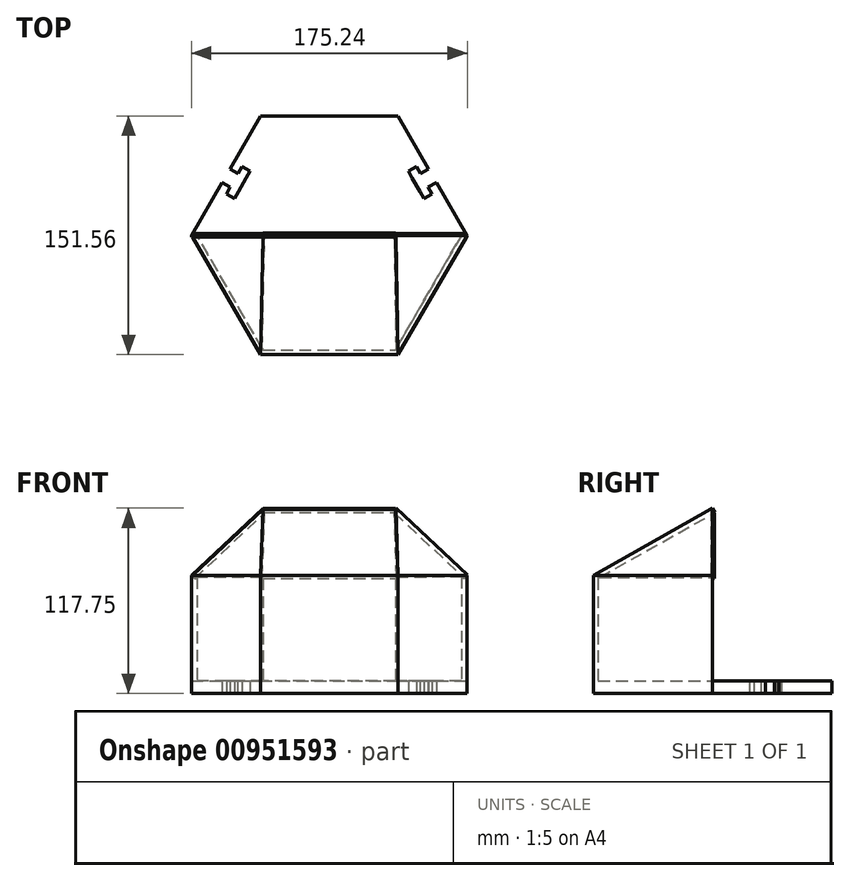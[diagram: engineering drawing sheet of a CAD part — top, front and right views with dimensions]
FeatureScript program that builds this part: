
annotation { "Feature Type Name" : "Feature", "Feature Type Description" : "" }
export const myFeature = defineFeature(function(context is Context, id is Id, definition is map)
    precondition{}
    {
        {
            var Q0;
            Q0=qCreatedBy(makeId("Top.planeOp"),FACE);
            var sketch = newSketch(context, id + "F0", { "sketchPlane" : qUnion([Q0])});
            skCircle(sketch, "E0.cCircle", {"center": v(0, 0) * mm, "radius": 75.78 * mm, "construction": true});
            skLineSegment(sketch, "E0.0", {"start": v(-43.75, 75.78) * mm, "end": v(43.75, 75.78) * mm});
            skLineSegment(sketch, "E0.1", {"start": v(43.75, 75.78) * mm, "end": v(87.5, 0) * mm});
            skLineSegment(sketch, "E0.2", {"start": v(87.5, 0) * mm, "end": v(43.75, -75.78) * mm});
            skLineSegment(sketch, "E0.3", {"start": v(43.75, -75.78) * mm, "end": v(-43.75, -75.78) * mm});
            skLineSegment(sketch, "E0.4", {"start": v(-43.75, -75.78) * mm, "end": v(-87.5, 0) * mm});
            skLineSegment(sketch, "E0.5", {"start": v(-87.5, 0) * mm, "end": v(-43.75, 75.78) * mm});
            skPoint(sketch, "E0.0.midPoint", {"position": v(0, 75.78) * mm});
            skLineSegment(sketch, "E1.0", {"start": v(-84.04, 0) * mm, "end": v(-42.02, 72.78) * mm});
            skLineSegment(sketch, "E1.1", {"start": v(42.02, 72.78) * mm, "end": v(84.04, 0) * mm});
            skLineSegment(sketch, "E1.2", {"start": v(84.04, 0) * mm, "end": v(42.02, -72.78) * mm});
            skLineSegment(sketch, "E1.3", {"start": v(-42.02, 72.78) * mm, "end": v(42.02, 72.78) * mm});
            skLineSegment(sketch, "E1.4", {"start": v(42.02, -72.78) * mm, "end": v(-42.02, -72.78) * mm});
            skLineSegment(sketch, "E1.5", {"start": v(-42.02, -72.78) * mm, "end": v(-84.04, 0) * mm});
            skLineSegment(sketch, "E2", {"start": v(-87.5, 0) * mm, "end": v(-84.04, 0) * mm});
            skLineSegment(sketch, "E3", {"start": v(84.04, 0) * mm, "end": v(87.5, 0) * mm});
            skLineSegment(sketch, "E4", {"start": v(0, 0) * mm, "end": v(0, 72.78) * mm, "construction": true});
            skLineSegment(sketch, "E5", {"start": v(0, 0) * mm, "end": v(42.02, 72.78) * mm, "construction": true});
            skLineSegment(sketch, "E6", {"start": v(0, 0) * mm, "end": v(-42.02, 72.78) * mm, "construction": true});
            skLineSegment(sketch, "E7", {"start": v(0, 36.39) * mm, "end": v(0, 72.78) * mm, "construction": true});
            skLineSegment(sketch, "E8.bottom", {"start": v(25, 48.33) * mm, "end": v(-25, 48.33) * mm});
            skLineSegment(sketch, "E8.top", {"start": v(25, 60.83) * mm, "end": v(-25, 60.83) * mm});
            skLineSegment(sketch, "E8.left", {"start": v(25, 48.33) * mm, "end": v(25, 60.83) * mm});
            skLineSegment(sketch, "E8.right", {"start": v(-25, 48.33) * mm, "end": v(-25, 60.83) * mm});
            skPoint(sketch, "E8.middle", {"position": v(0, 54.58) * mm});
            skLineSegment(sketch, "E9", {"start": v(-65.63, 37.89) * mm, "end": v(-55.16, 32) * mm, "construction": true});
            skLineSegment(sketch, "E10", {"start": v(-55.16, 32) * mm, "end": v(-52.71, 36.37) * mm, "construction": true});
            skLineSegment(sketch, "E11", {"start": v(-55.16, 32) * mm, "end": v(-57.62, 27.65) * mm, "construction": true});
            skLineSegment(sketch, "E12", {"start": v(-52.71, 36.37) * mm, "end": v(-63.12, 42.22) * mm});
            skLineSegment(sketch, "E13", {"start": v(-57.62, 27.65) * mm, "end": v(-52.71, 36.37) * mm});
            skLineSegment(sketch, "E14", {"start": v(-65.63, 37.89) * mm, "end": v(-68.13, 33.56) * mm});
            skLineSegment(sketch, "E15", {"start": v(-57.62, 27.65) * mm, "end": v(-68.13, 33.56) * mm});
            skLineSegment(sketch, "E16.MirrorCS", {"start": v(55.16, 32) * mm, "end": v(57.62, 27.65) * mm});
            skLineSegment(sketch, "E17.MirrorCS", {"start": v(55.16, 32) * mm, "end": v(52.71, 36.37) * mm});
            skLineSegment(sketch, "E18.MirrorCS", {"start": v(57.62, 27.65) * mm, "end": v(68.13, 33.56) * mm});
            skLineSegment(sketch, "E19.MirrorCS", {"start": v(87.5, 0) * mm, "end": v(43.75, 75.78) * mm});
            skLineSegment(sketch, "E20.MirrorCS", {"start": v(52.71, 36.37) * mm, "end": v(63.12, 42.22) * mm});
            skLineSegment(sketch, "E21", {"start": v(-62.87, 30.6) * mm, "end": v(-65.32, 26.25) * mm});
            skLineSegment(sketch, "E22", {"start": v(-57.62, 27.65) * mm, "end": v(-60.07, 23.3) * mm});
            skLineSegment(sketch, "E23", {"start": v(-65.32, 26.25) * mm, "end": v(-60.07, 23.3) * mm});
            skLineSegment(sketch, "E24.MirrorCS", {"start": v(-52.71, 36.37) * mm, "end": v(-50.26, 40.72) * mm});
            skLineSegment(sketch, "E25.MirrorCS", {"start": v(-57.97, 39.32) * mm, "end": v(-55.52, 43.68) * mm});
            skLineSegment(sketch, "E26.MirrorCS", {"start": v(-55.52, 43.68) * mm, "end": v(-50.26, 40.72) * mm});
            skLineSegment(sketch, "E27.MirrorCS", {"start": v(57.97, 39.32) * mm, "end": v(55.52, 43.68) * mm});
            skLineSegment(sketch, "E28.MirrorCS", {"start": v(55.52, 43.68) * mm, "end": v(50.26, 40.72) * mm});
            skLineSegment(sketch, "E29.MirrorCS", {"start": v(52.71, 36.37) * mm, "end": v(50.26, 40.72) * mm});
            skLineSegment(sketch, "E30.MirrorCS", {"start": v(57.62, 27.65) * mm, "end": v(60.07, 23.3) * mm});
            skLineSegment(sketch, "E31.MirrorCS", {"start": v(62.87, 30.6) * mm, "end": v(65.32, 26.25) * mm});
            skLineSegment(sketch, "E32.MirrorCS", {"start": v(65.32, 26.25) * mm, "end": v(60.07, 23.3) * mm});
            skLineSegment(sketch, "E33", {"start": v(-68.13, 33.56) * mm, "end": v(-65.5, 32.09) * mm});
            skLineSegment(sketch, "E34", {"start": v(68.13, 33.56) * mm, "end": v(65.5, 32.09) * mm});
            skSolve(sketch);
        }
        {
            var Q0;
            Q0=makeQuery(id+"F0.imprint","IMPRINT",FACE,{"disambiguationData":[TD([[makeQuery(id+"F0.imprint","IMPRINT",EDGE,{"derivedFrom":sQuery(id+"F0.wireOp",EDGE,"E1.0")}),-1.0]])]});
            extrude(context, id + "F1", {"entities" : qUnion([Q0]), "depth" : 8 * mm, "offsetDistance" : 25 * mm});
        }
        {
            var Q0;
            Q0=makeQuery(id+"F0.imprint","IMPRINT",FACE,{"disambiguationData":[TD([[makeQuery(id+"F0.imprint","IMPRINT",EDGE,{"derivedFrom":sQuery(id+"F0.wireOp",EDGE,"E0.2")}),-1.0]])]});
            extrude(context, id + "F2", {"entities" : qUnion([Q0]), "operationType" : NewBodyOperationType.ADD, "depth" : 75 * mm, "offsetDistance" : 25 * mm});
        }
        {
            var Q0;
            Q0=qCreatedBy(makeId("Front.planeOp"),FACE);
            var sketch = newSketch(context, id + "F3", { "sketchPlane" : qUnion([Q0])});
            skLineSegment(sketch, "E35", {"start": v(0, 0) * mm, "end": v(0, 144.27) * mm, "construction": true});
            skLineSegment(sketch, "E36", {"start": v(0, 144.27) * mm, "end": v(-94, 144.27) * mm, "construction": true});
            skLineSegment(sketch, "E37", {"start": v(0, 144.27) * mm, "end": v(81.74, 144.27) * mm});
            skLineSegment(sketch, "E38", {"start": v(0, 0) * mm, "end": v(0, 75) * mm, "construction": true});
            skLineSegment(sketch, "E39", {"start": v(0, 75) * mm, "end": v(0, 114.5) * mm, "construction": true});
            skLineSegment(sketch, "E40", {"start": v(0, 75) * mm, "end": v(-87.5, 75) * mm, "construction": true});
            skLineSegment(sketch, "E41", {"start": v(0, 114.5) * mm, "end": v(42.02, 114.5) * mm, "construction": true});
            skLineSegment(sketch, "E42", {"start": v(0, 114.5) * mm, "end": v(-42.02, 114.5) * mm});
            skLineSegment(sketch, "E43", {"start": v(0, 75) * mm, "end": v(-84.04, 75) * mm, "construction": true});
            skLineSegment(sketch, "E44", {"start": v(-42.02, 114.5) * mm, "end": v(-84.04, 75) * mm});
            skLineSegment(sketch, "E45", {"start": v(-42.02, 114.5) * mm, "end": v(-42.02, 117.5) * mm, "construction": true});
            skLineSegment(sketch, "E46", {"start": v(-42.02, 117.5) * mm, "end": v(-87.5, 75) * mm});
            skLineSegment(sketch, "E47", {"start": v(-42.02, 117.5) * mm, "end": v(0, 117.5) * mm});
            skLineSegment(sketch, "E48.MirrorCS", {"start": v(42.02, 117.5) * mm, "end": v(87.5, 75) * mm});
            skLineSegment(sketch, "E49.MirrorCS", {"start": v(42.02, 114.5) * mm, "end": v(84.04, 75) * mm});
            skLineSegment(sketch, "E50.MirrorCS", {"start": v(42.02, 117.5) * mm, "end": v(0, 117.5) * mm});
            skLineSegment(sketch, "E51.MirrorCS", {"start": v(0, 114.5) * mm, "end": v(42.02, 114.5) * mm});
            skLineSegment(sketch, "E52", {"start": v(87.5, 75) * mm, "end": v(84.04, 75) * mm});
            skLineSegment(sketch, "E53", {"start": v(-84.04, 75) * mm, "end": v(-87.5, 75) * mm});
            skSolve(sketch);
        }
        {
            var Q0;
            Q0=makeQuery(id+"F0.imprint","IMPRINT",FACE,{"disambiguationData":[TD([[makeQuery(id+"F0.imprint","IMPRINT",EDGE,{"derivedFrom":sQuery(id+"F0.wireOp",EDGE,"E0.0")}),-1.0]])]});
            extrude(context, id + "F4", {"entities" : qUnion([Q0]), "operationType" : NewBodyOperationType.ADD, "oppositeDirection" : true, "depth" : -8 * mm, "offsetDistance" : 25 * mm});
        }
        {
            var Q0;
            Q0=makeQuery(id+"F2.opExtrude","CAP_EDGE",EDGE,{"disambiguationData":[OSD([sQuery(id+"F0.wireOp",EDGE,"E0.3")])],"isStart":false});
            var Q1;
            Q1=sQuery(id+"F3.wireOp",VERTEX,"E47.end");
            cPlane(context, id + "F5", {"entities" : qUnion([Q0, Q1]), "cplaneType" : CPlaneType.LINE_ANGLE, "offset" : 25 * mm, "angle" : 0 * degree, "width" : 150 * mm, "height" : 150 * mm});
        }
        {
            var Q0;
            Q0=qCreatedBy(id+"F5.planeOp",FACE);
            var sketch = newSketch(context, id + "F6", { "sketchPlane" : qUnion([Q0])});
            skLineSegment(sketch, "E54", {"start": v(0, 29.4) * mm, "end": v(43.75, 29.4) * mm});
            skLineSegment(sketch, "E55", {"start": v(0, 29.4) * mm, "end": v(-43.75, 29.4) * mm});
            skLineSegment(sketch, "E56", {"start": v(-43.75, 29.4) * mm, "end": v(-42.02, -57.48) * mm});
            skLineSegment(sketch, "E57", {"start": v(43.75, 29.4) * mm, "end": v(42.02, -57.48) * mm});
            skLineSegment(sketch, "E58", {"start": v(-42.02, -57.48) * mm, "end": v(42.02, -57.48) * mm});
            skSolve(sketch);
        }
        {
            var Q0;
            Q0=makeQuery(id+"F6.imprint","IMPRINT",FACE,{"disambiguationData":[TD([[makeQuery(id+"F6.imprint","IMPRINT",EDGE,{"derivedFrom":sQuery(id+"F6.wireOp",EDGE,"E54")}),-1.0]])]});
            extrude(context, id + "F7", {"entities" : qUnion([Q0]), "operationType" : NewBodyOperationType.ADD, "depth" : 3 * mm, "offsetDistance" : 25 * mm});
        }
        {
            var Q0;
            Q0=makeQuery(id+"F3.imprint","IMPRINT",FACE,{"disambiguationData":[TD([[makeQuery(id+"F3.imprint","IMPRINT",EDGE,{"derivedFrom":sQuery(id+"F3.wireOp",EDGE,"E42")}),-1.0]])]});
            extrude(context, id + "F8", {"entities" : qUnion([Q0]), "operationType" : NewBodyOperationType.ADD, "depth" : 1 * mm, "offsetDistance" : 25 * mm});
        }
        {
            var Q0;
            Q0=makeQuery(id+"F8.opExtrude","CAP_EDGE",EDGE,{"disambiguationData":[OSD([sQuery(id+"F3.wireOp",EDGE,"E46")])],"isStart":true});
            var Q1;
            Q1=makeQuery(id+"F7.boolean.opBoolean","MERGE",VERTEX,{"derivedFrom":[makeQuery(id+"F2.opExtrude","CAP_VERTEX",VERTEX,{"disambiguationData":[OSD([sQuery(id+"F0.wireOp",EDGE,"E0.3"),sQuery(id+"F0.wireOp",EDGE,"E0.4")])],"isStart":false}),makeQuery(id+"F7.opExtrude","CAP_VERTEX",VERTEX,{"disambiguationData":[OSD([sQuery(id+"F6.wireOp",EDGE,"E55"),sQuery(id+"F6.wireOp",EDGE,"E56")])],"isStart":true})]});
            cPlane(context, id + "F9", {"entities" : qUnion([Q0, Q1]), "cplaneType" : CPlaneType.LINE_ANGLE, "offset" : 25 * mm, "angle" : 0 * degree, "width" : 150 * mm, "height" : 150 * mm});
        }
        {
            var Q0;
            Q0=qCreatedBy(id+"F9.planeOp",FACE);
            var sketch = newSketch(context, id + "F10", { "sketchPlane" : qUnion([Q0])});
            skLineSegment(sketch, "E59", {"start": v(-25.66, 35.61) * mm, "end": v(30.99, -31.08) * mm});
            skLineSegment(sketch, "E60", {"start": v(-25.66, 35.61) * mm, "end": v(33.23, 55.79) * mm});
            skLineSegment(sketch, "E61", {"start": v(33.23, 55.79) * mm, "end": v(30.99, -31.08) * mm});
            skSolve(sketch);
        }
        {
            var Q0;
            Q0=qSketchRegion(id+"F10",true);
            extrude(context, id + "F11", {"entities" : qUnion([Q0]), "operationType" : NewBodyOperationType.ADD, "depth" : -3 * mm, "offsetDistance" : 25 * mm});
        }
        {
            var Q0;
            Q0=makeQuery(id+"F8.opExtrude","CAP_EDGE",EDGE,{"disambiguationData":[OSD([sQuery(id+"F3.wireOp",EDGE,"E48.MirrorCS")])],"isStart":false});
            var Q1;
            Q1=makeQuery(id+"F7.boolean.opBoolean","MERGE",VERTEX,{"derivedFrom":[makeQuery(id+"F2.opExtrude","CAP_VERTEX",VERTEX,{"disambiguationData":[OSD([sQuery(id+"F0.wireOp",EDGE,"E0.2"),sQuery(id+"F0.wireOp",EDGE,"E0.3")])],"isStart":false}),makeQuery(id+"F7.opExtrude","CAP_VERTEX",VERTEX,{"disambiguationData":[OSD([sQuery(id+"F6.wireOp",EDGE,"E54"),sQuery(id+"F6.wireOp",EDGE,"E57")])],"isStart":true})]});
            cPlane(context, id + "F12", {"entities" : qUnion([Q0, Q1]), "cplaneType" : CPlaneType.LINE_ANGLE, "offset" : 25 * mm, "angle" : 0 * degree, "width" : 150 * mm, "height" : 150 * mm});
        }
        {
            var Q0;
            Q0=qCreatedBy(id+"F12.planeOp",FACE);
            var sketch = newSketch(context, id + "F13", { "sketchPlane" : qUnion([Q0])});
            skLineSegment(sketch, "E62", {"start": v(-32.88, -56.36) * mm, "end": v(25.94, -35.98) * mm});
            skLineSegment(sketch, "E63", {"start": v(25.94, -35.98) * mm, "end": v(-30.94, 30.51) * mm});
            skLineSegment(sketch, "E64", {"start": v(-30.94, 30.51) * mm, "end": v(-32.88, -56.36) * mm});
            skSolve(sketch);
        }
        {
            var Q0;
            Q0=qSketchRegion(id+"F13",true);
            extrude(context, id + "F14", {"entities" : qUnion([Q0]), "operationType" : NewBodyOperationType.ADD, "depth" : 3 * mm, "offsetDistance" : 25 * mm});
        }
        {
            var Q0;
            Q0=makeQuery(id+"F0.imprint","IMPRINT",FACE,{"disambiguationData":[TD([[makeQuery(id+"F0.imprint","IMPRINT",EDGE,{"derivedFrom":sQuery(id+"F0.wireOp",EDGE,"E8.bottom")}),-1.0]])]});
            extrude(context, id + "F15", {"entities" : qUnion([Q0]), "operationType" : NewBodyOperationType.ADD, "depth" : 8 * mm, "offsetDistance" : 25 * mm});
        }
        {
            var Q0;
            {var subQ5=sQuery(id+"F0.wireOp",EDGE,"E13");Q0=makeQuery(id+"F0.imprint","IMPRINT",FACE,{"disambiguationData":[TD([[makeQuery(id+"F0.imprint","IMPRINT",EDGE,{"derivedFrom":subQ5}),1.0]])]});}
            var Q1;
            {var subQ5=sQuery(id+"F0.wireOp",EDGE,"ALQEQqr1-oKlR-f4O9-fg5D-6GHPOLekQC52");Q1=makeQuery(id+"F0.imprint","IMPRINT",FACE,{"disambiguationData":[TD([[makeQuery(id+"F0.imprint","IMPRINT",EDGE,{"derivedFrom":subQ5}),-1.0]])]});}
            extrude(context, id + "F16", {"entities" : qUnion([Q0, Q1]), "operationType" : NewBodyOperationType.REMOVE, "oppositeDirection" : true, "depth" : 25 * mm, "offsetDistance" : 25 * mm});
        }
        {
            var Q0;
            {var subQ0=sQuery(id+"F0.wireOp",EDGE,"E2");Q0=makeQuery(id+"F0.imprint","IMPRINT",FACE,{"disambiguationData":[TD([[makeQuery(id+"F0.imprint","IMPRINT",EDGE,{"derivedFrom":subQ0}),1.0]])]});}
            var Q1;
            {var subQ0=sQuery(id+"F0.wireOp",EDGE,"E3");Q1=makeQuery(id+"F0.imprint","IMPRINT",FACE,{"disambiguationData":[TD([[makeQuery(id+"F0.imprint","IMPRINT",EDGE,{"derivedFrom":subQ0}),1.0]])]});}
            extrude(context, id + "F17", {"entities" : qUnion([Q0, Q1]), "operationType" : NewBodyOperationType.ADD, "depth" : 8 * mm, "offsetDistance" : 25 * mm});
        }
    });
